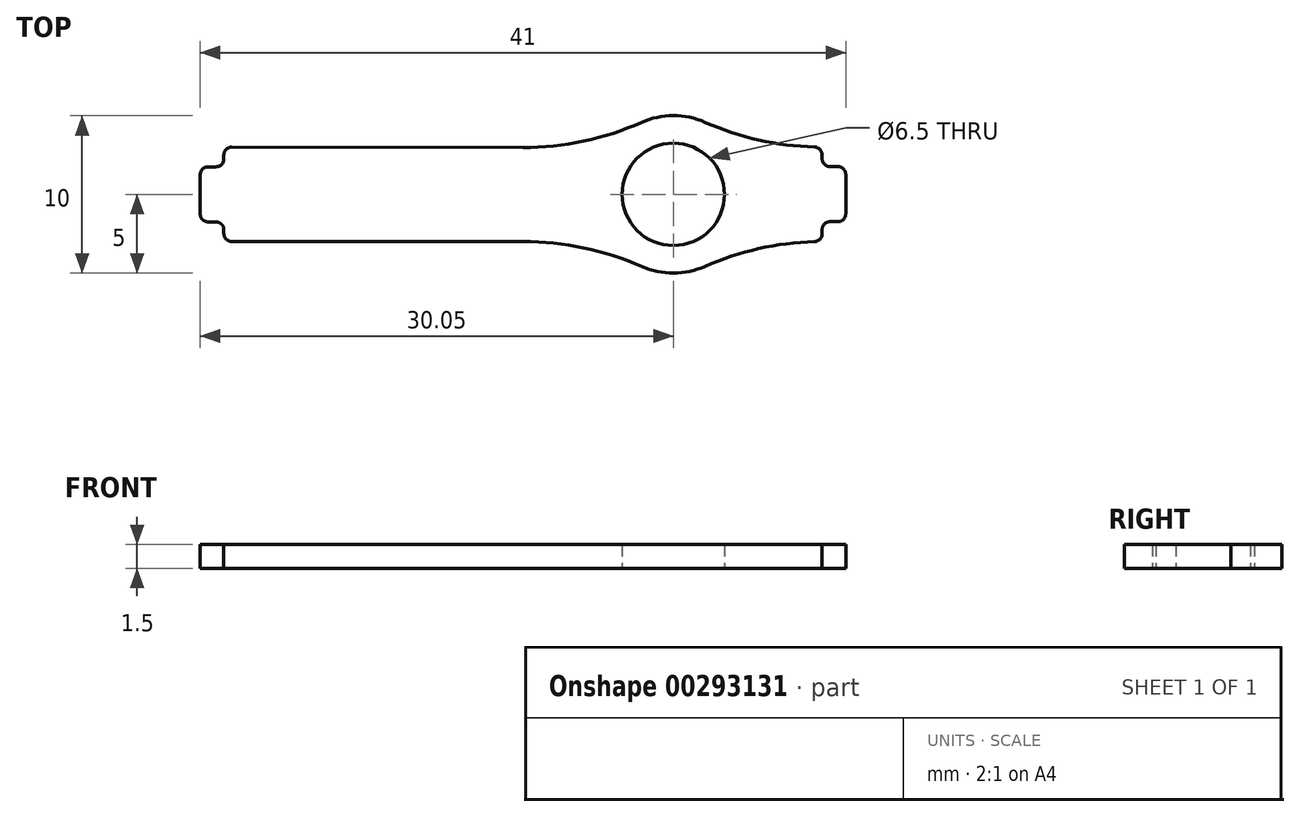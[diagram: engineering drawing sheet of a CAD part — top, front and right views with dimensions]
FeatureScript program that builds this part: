
annotation { "Feature Type Name" : "Feature", "Feature Type Description" : "" }
export const myFeature = defineFeature(function(context is Context, id is Id, definition is map)
    precondition{}
    {
        {
            var Q0;
            Q0=qCreatedBy(makeId("Top.planeOp"),FACE);
            var sketch = newSketch(context, id + "F0", { "sketchPlane" : qUnion([Q0])});
            skArc(sketch, "E0", {"start": v(18.51, -3) * mm, "mid": v(14.97, -3.45) * mm, "end": v(11.58, -4.57) * mm});
            skArc(sketch, "E1", {"start": v(7.54, -4.58) * mm, "mid": v(9.56, -5) * mm, "end": v(11.58, -4.57) * mm});
            skArc(sketch, "E2", {"start": v(7.54, -4.58) * mm, "mid": v(3.85, -3.4) * mm, "end": v(0, -3) * mm});
            skLineSegment(sketch, "E3", {"start": v(0, -3) * mm, "end": v(-18.5, -3) * mm});
            skArc(sketch, "E4", {"start": v(-18.5, 3) * mm, "mid": v(-18.5, 3) * mm, "end": v(-18.5, 3) * mm});
            skLineSegment(sketch, "E5", {"start": v(-18.5, 3) * mm, "end": v(0, 2.98) * mm});
            skArc(sketch, "E6", {"start": v(0, 2.98) * mm, "mid": v(3.84, 3.38) * mm, "end": v(7.52, 4.57) * mm});
            skArc(sketch, "E7", {"start": v(11.58, 4.57) * mm, "mid": v(9.55, 5) * mm, "end": v(7.52, 4.57) * mm});
            skArc(sketch, "E8", {"start": v(11.58, 4.57) * mm, "mid": v(14.97, 3.45) * mm, "end": v(18.51, 3) * mm});
            skCircle(sketch, "E9", {"center": v(9.55, 0) * mm, "radius": 3.25 * mm});
            skLineSegment(sketch, "E10", {"start": v(20.5, 0.01) * mm, "end": v(20.5, -1.24) * mm});
            skLineSegment(sketch, "E11", {"start": v(20.5, 0.01) * mm, "end": v(20.5, 1.26) * mm});
            skLineSegment(sketch, "E12", {"start": v(19.5, -1.74) * mm, "end": v(20, -1.74) * mm});
            skArc(sketch, "E13", {"start": v(19.5, -1.74) * mm, "mid": v(19.15, -1.88) * mm, "end": v(19, -2.24) * mm});
            skArc(sketch, "E14", {"start": v(19, 2.5) * mm, "mid": v(18.86, 2.86) * mm, "end": v(18.51, 3) * mm});
            skLineSegment(sketch, "E15", {"start": v(19, -2.5) * mm, "end": v(19, -2.24) * mm});
            skArc(sketch, "E16", {"start": v(18.51, -3) * mm, "mid": v(18.86, -2.86) * mm, "end": v(19, -2.5) * mm});
            skArc(sketch, "E17", {"start": v(-18.5, 3) * mm, "mid": v(-18.85, 2.85) * mm, "end": v(-19, 2.5) * mm});
            skLineSegment(sketch, "E18", {"start": v(-19, -2.5) * mm, "end": v(-19, -2.25) * mm});
            skArc(sketch, "E19", {"start": v(-19, -2.5) * mm, "mid": v(-18.85, -2.85) * mm, "end": v(-18.5, -3) * mm});
            skArc(sketch, "E20", {"start": v(20, -1.74) * mm, "mid": v(20.35, -1.59) * mm, "end": v(20.5, -1.24) * mm});
            skLineSegment(sketch, "E21", {"start": v(20, 1.76) * mm, "end": v(19.5, 1.76) * mm});
            skArc(sketch, "E22", {"start": v(20.5, 1.26) * mm, "mid": v(20.35, 1.62) * mm, "end": v(20, 1.76) * mm});
            skLineSegment(sketch, "E23", {"start": v(-20, 1.75) * mm, "end": v(-19.5, 1.75) * mm});
            skLineSegment(sketch, "E24", {"start": v(-20.5, 1.25) * mm, "end": v(-20.5, 0) * mm});
            skArc(sketch, "E25", {"start": v(-20, 1.75) * mm, "mid": v(-20.35, 1.6) * mm, "end": v(-20.5, 1.25) * mm});
            skLineSegment(sketch, "E26", {"start": v(-20.5, -1.25) * mm, "end": v(-20.5, 0) * mm});
            skArc(sketch, "E27", {"start": v(-20.5, -1.25) * mm, "mid": v(-20.35, -1.6) * mm, "end": v(-20, -1.75) * mm});
            skLineSegment(sketch, "E28", {"start": v(-19.5, -1.75) * mm, "end": v(-20, -1.75) * mm});
            skArc(sketch, "E29", {"start": v(-19, -2.25) * mm, "mid": v(-19.15, -1.9) * mm, "end": v(-19.5, -1.75) * mm});
            skLineSegment(sketch, "E30", {"start": v(-19, 2.25) * mm, "end": v(-19, 2.5) * mm});
            skArc(sketch, "E31", {"start": v(-19.5, 1.75) * mm, "mid": v(-19.15, 1.9) * mm, "end": v(-19, 2.25) * mm});
            skLineSegment(sketch, "E32", {"start": v(19, 2.26) * mm, "end": v(19, 2.5) * mm});
            skArc(sketch, "E33", {"start": v(19, 2.26) * mm, "mid": v(19.15, 1.9) * mm, "end": v(19.5, 1.76) * mm});
            skSolve(sketch);
        }
        {
            var Q0;
            Q0 = qSketchRegion(id + "F0", true);
            extrude(context, id + "F1", {"entities" : qUnion([Q0]), "depth" : 1.5 * mm});
        }
    });
